# Revit family: Sanitary_Taps-And-Mixers_Sanindusa_Torus-Thermostatic-Shower-Kit
name_source: partatom
category: Plumbing Fixtures
revit_build: Autodesk Revit 2018 (Build: 20170223_1515(x64)
units: mm (PartAtom-declared; Revit-internal decimal feet)

## family parameters
Always vertical = Yes
Cut with Voids When Loaded = No
OmniClass Number = 23.45.00.00
OmniClass Title = Sanitary, Laundry, and Cleaning Equipment
Part Type = Normal
Room Calculation Point = No
Round Connector Dimension = Use Diameter
Shared = No
Work Plane-Based = No

## types (1)
- Sanitary_Taps-And-Mixers_Sanindusa_Torus-Thermostatic-Shower-Kit
    AssetType = Fixed
    BodyMaterial = Brass
    CartridgeType = Thermostatic cartridge
    Color = Silver
    Constituents = Thermostatic Mixer; 180 mm Face ABS head shower, with spherical swivel 45º; Duo ABS hand shower;
150 mm PVC flexible hose; ABS shower bracket, with adjustable height; Fixing Kit.
    Cost = 0 $
    Description = Torus thermostatic shower kit
    Edition number = 1
    Element Type = FAUCET: A small diameter valve, with a free outlet, from which water is drawn.
    FaucetFunction = Mixed
    FaucetOperation = Other
    FaucetTopDescription = Hand wheel
    FaucetType = SprayMixing
    Features = Thermostatic cartridge technology. With temperature limiter at 38ºC (for higher temperatures it is necessary to press the button to unlock the safety mode). Protection against scalding (dual-chamber tub). Superior arm with rotation angle of 45°. Automatic shut off in the event of hot or cold water supply failure.
Complete shower system, easy to install, ideal for bathroom renovation projects.
    Finish = Chrome plated
    FittingCentres = 150 mm
    FlowCoefficient = water flow to 3 bar**: 12L/min.
(** 38°C)
    FlowRateMaximum = 17 L/min at 3 bar
    InletConnectionType = Eccentric G 1/2" - 3/4
    Installation Instructions = https://www.tec.sanindusa.pt
    InstallationDate = 1900-12-31T23:59:59
    Manufacturer = Sanindusa
    ManufacturerName = Sanindusa
    ManufacturerURL = www.tec.sanindusa.pt
    Material = Brass
    ModelNumber = 537772111
    ModelReference = Torus
    Name = Torus thermostatic shower kit
    NominalHeight = 1162 mm  [stored 3.81234 ft]
    NominalLength = 280 mm  [stored 0.918635 ft]
    NominalWidth = 560 mm  [stored 1.83727 ft]
    OperatingMechanismMaterial = Brass
    OutletConnectionType = M12x1 - G 1/2"
    Pre-defined type (IFC) = FAUCET
    Product Guid = 397e3a74-e507-4052-8033-4a7b67eb643c
    Product data url = https://bimobject.com
    ProductInformation = https://www.tec.sanindusa.pt
    ProductionYear = 2017
    Size = 280x560x1162
    TestPressure = 10 bar
    Type (IFC) = IfcValveType
    URL = www.tec.sanindusa.pt
    Uniclass2015Version = Products v1.6
    ValveMechanism = UNSET
    ValveOperation = THERMOSTATIC
    ValvePattern = UNSET
    Version = 2
    WarrantyDescription = https://www.tec.sanindusa.pt
    WarrantyDurationParts = 5
    WarrantyDurationUnit = year
    WarrantyStartDate = 1900-12-31T23:59:59
1900-12-31T23:59:59
    WaterSuplyTemperatureMaximum = 80°C
    Weight = 5.00 kg
    WorkingPressure = 0.5 - 3 bar

note: [stored X ft] marks values corroborated as IEEE doubles in the binary element streams (Revit-internal decimal feet)

## geometry (parser evidence)
native form markers: Sweep x7
no freeform markers — native parametric forms only
